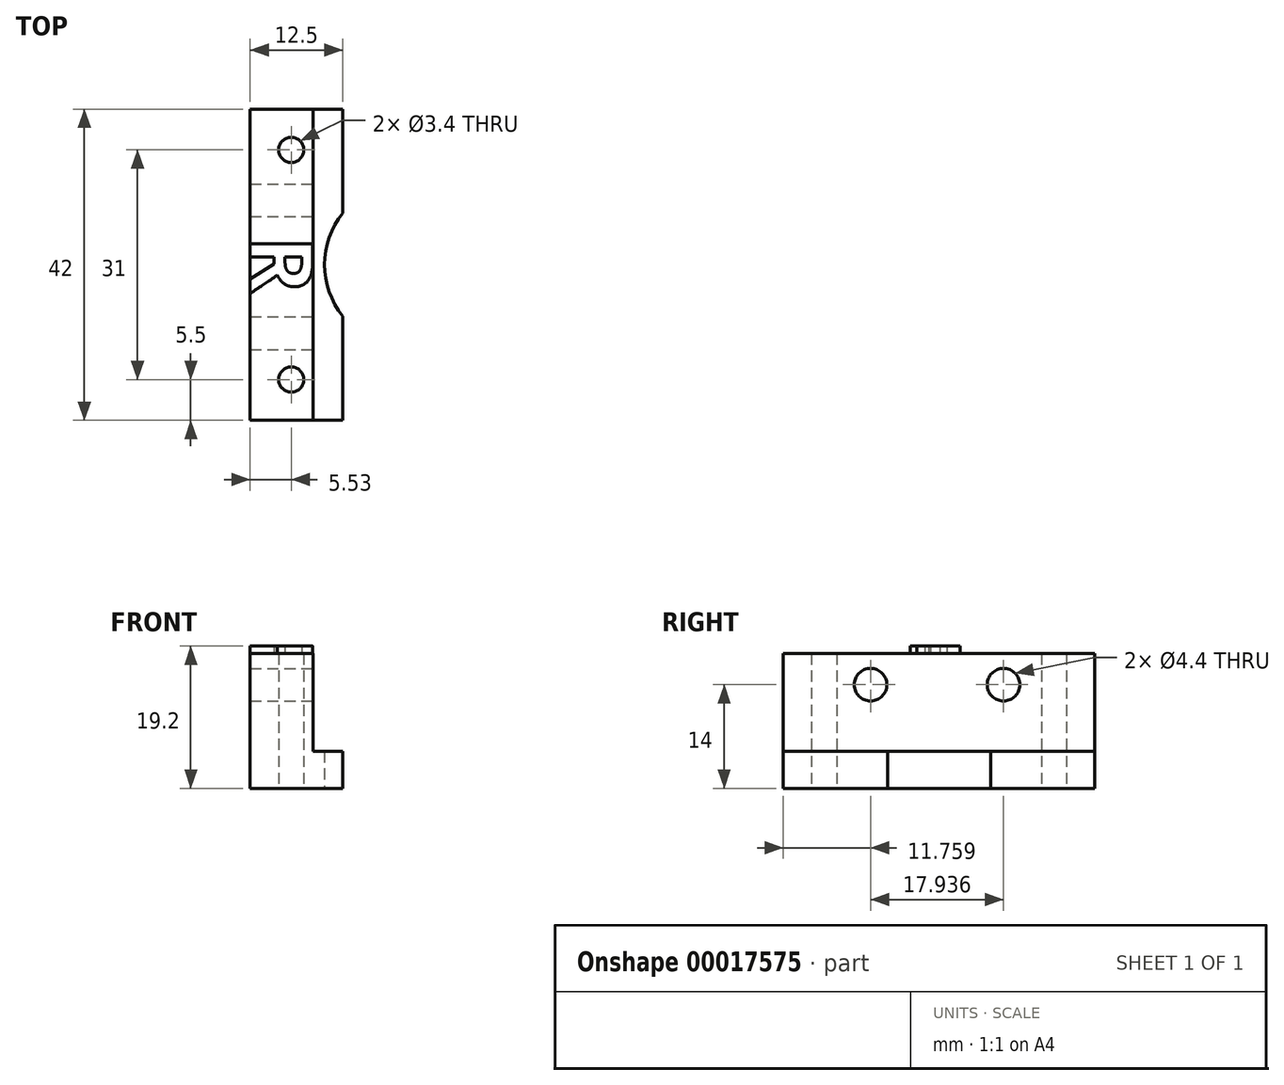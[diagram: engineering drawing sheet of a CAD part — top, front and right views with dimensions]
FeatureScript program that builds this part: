
annotation { "Feature Type Name" : "Feature", "Feature Type Description" : "" }
export const myFeature = defineFeature(function(context is Context, id is Id, definition is map)
    precondition{}
    {
        {
            var Q0;
            Q0=qCreatedBy(makeId("Front.planeOp"),FACE);
            var sketch = newSketch(context, id + "F0", { "sketchPlane" : qUnion([Q0])});
            skLineSegment(sketch, "E0", {"start": v(8.5, 18.2) * mm, "end": v(8.5, 5) * mm});
            skLineSegment(sketch, "E1", {"start": v(8.5, 5) * mm, "end": v(12.5, 5) * mm});
            skLineSegment(sketch, "E2", {"start": v(12.5, 5) * mm, "end": v(12.5, 0) * mm});
            skLineSegment(sketch, "E3", {"start": v(12.5, 0) * mm, "end": v(0, 0) * mm});
            skLineSegment(sketch, "E4", {"start": v(0, 0) * mm, "end": v(0, 18.2) * mm});
            skLineSegment(sketch, "E5", {"start": v(0, 18.2) * mm, "end": v(8.5, 18.2) * mm});
            skSolve(sketch);
        }
        {
            var Q0;
            Q0=qSketchRegion(id+"F0",true);
            extrude(context, id + "F1", {"entities" : qUnion([Q0]), "oppositeDirection" : true, "depth" : 42 * mm});
        }
        {
            var Q0;
            Q0=makeQuery(id+"F1.opExtrude","SWEPT_FACE",FACE,{"disambiguationData":[OSD([sQuery(id+"F0.wireOp",EDGE,"E3")])]});
            var sketch = newSketch(context, id + "F2", { "sketchPlane" : qUnion([Q0])});
            skCircle(sketch, "E6", {"center": v(5.53, -5.5) * mm, "radius": 1.7 * mm});
            skCircle(sketch, "E7", {"center": v(5.53, -36.5) * mm, "radius": 1.7 * mm});
            skCircle(sketch, "E8", {"center": v(21.03, -21) * mm, "radius": 11 * mm});
            skLineSegment(sketch, "E9", {"start": v(0, -21) * mm, "end": v(12.5, -21) * mm, "construction": true});
            skSolve(sketch);
        }
        {
            var Q0;
            Q0=qSketchRegion(id+"F2",true);
            extrude(context, id + "F3", {"entities" : qUnion([Q0]), "operationType" : NewBodyOperationType.REMOVE, "endBound" : BoundingType.THROUGH_ALL, "oppositeDirection" : true, "depth" : 25 * mm});
        }
        {
            var Q0;
            Q0=makeQuery(id+"F1.opExtrude","SWEPT_FACE",FACE,{"disambiguationData":[OSD([sQuery(id+"F0.wireOp",EDGE,"E0")])]});
            var sketch = newSketch(context, id + "F4", { "sketchPlane" : qUnion([Q0])});
            skCircle(sketch, "E10", {"center": v(11.76, 14) * mm, "radius": 2.2 * mm});
            skCircle(sketch, "E11", {"center": v(29.7, 14) * mm, "radius": 2.2 * mm});
            skPoint(sketch, "E12", {"position": v(7.56, 18.2) * mm});
            skPoint(sketch, "E13", {"position": v(33.9, 18.2) * mm});
            skLineSegment(sketch, "E14", {"start": v(7.56, 18.2) * mm, "end": v(7.56, 10.72) * mm, "construction": true});
            skLineSegment(sketch, "E15", {"start": v(33.9, 18.2) * mm, "end": v(33.9, 12.44) * mm, "construction": true});
            skSolve(sketch);
        }
        {
            var Q0;
            Q0=qSketchRegion(id+"F4",true);
            extrude(context, id + "F5", {"entities" : qUnion([Q0]), "operationType" : NewBodyOperationType.REMOVE, "oppositeDirection" : true, "depth" : 25 * mm});
        }
        {
            var Q0;
            Q0=makeQuery(id+"F1.opExtrude","SWEPT_FACE",FACE,{"disambiguationData":[OSD([sQuery(id+"F0.wireOp",EDGE,"E5")])]});
            var sketch = newSketch(context, id + "F6", { "sketchPlane" : qUnion([Q0])});
            skText(sketch, "E16", { "text": "R", "fontName": "OpenSans-Bold.ttf"});
            const initialGuessF6  = {"E16": [0, 0.0249, 0, -1, 0.0085]};
            skSetInitialGuess(sketch, initialGuessF6);
            skSolve(sketch);
        }
        {
            var Q0;
            Q0=qSketchRegion(id+"F6",true);
            extrude(context, id + "F7", {"entities" : qUnion([Q0]), "operationType" : NewBodyOperationType.ADD, "depth" : 1 * mm});
        }
    });
